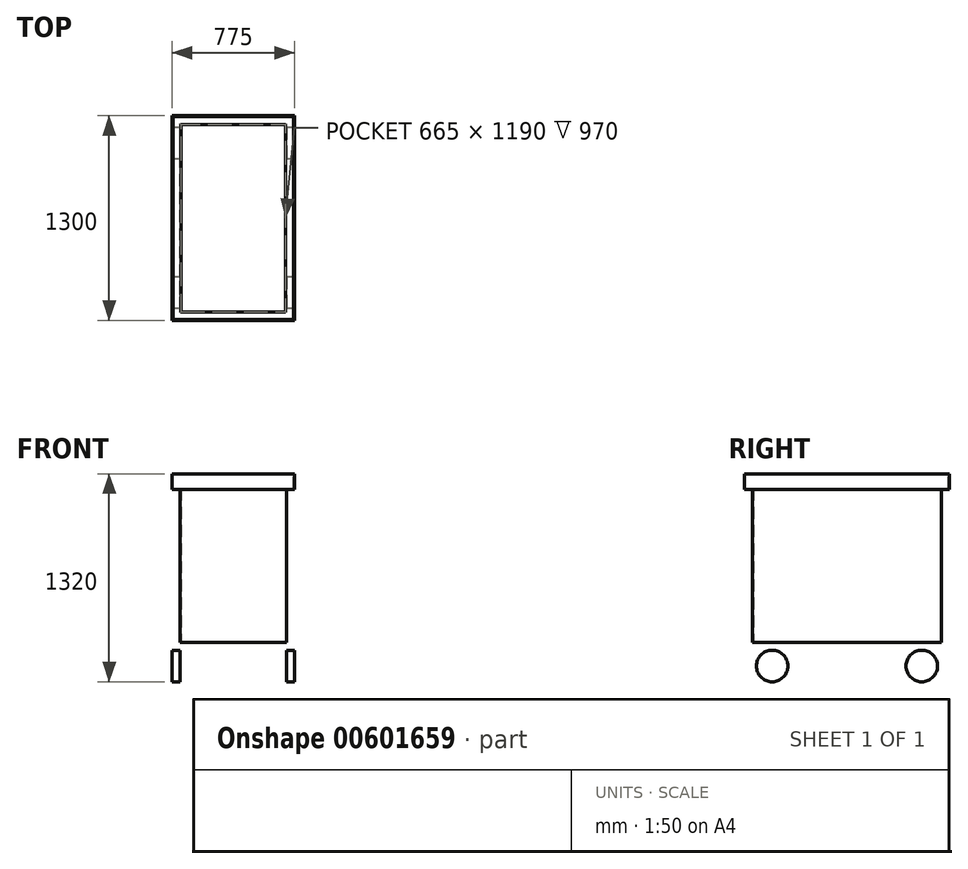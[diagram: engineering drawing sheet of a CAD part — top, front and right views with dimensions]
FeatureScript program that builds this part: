
annotation { "Feature Type Name" : "Feature", "Feature Type Description" : "" }
export const myFeature = defineFeature(function(context is Context, id is Id, definition is map)
    precondition{}
    {
        {
            var Q0;
            Q0=qCreatedBy(makeId("Top.planeOp"),FACE);
            cPlane(context, id + "F0", {"entities" : qUnion([Q0]), "cplaneType" : CPlaneType.OFFSET, "offset" : 250 * mm, "width" : 150 * mm, "height" : 150 * mm});
        }
        {
            var Q0;
            Q0=qCreatedBy(id+"F0.planeOp",FACE);
            var sketch = newSketch(context, id + "F1", { "sketchPlane" : qUnion([Q0])});
            skLineSegment(sketch, "E0.bottom", {"start": v(0, 0) * mm, "end": v(775, 0) * mm});
            skLineSegment(sketch, "E0.top", {"start": v(0, 1300) * mm, "end": v(775, 1300) * mm});
            skLineSegment(sketch, "E0.left", {"start": v(0, 0) * mm, "end": v(0, 1300) * mm});
            skLineSegment(sketch, "E0.right", {"start": v(775, 0) * mm, "end": v(775, 1300) * mm});
            skLineSegment(sketch, "E1.0", {"start": v(50, 50) * mm, "end": v(725, 50) * mm});
            skLineSegment(sketch, "E1.1", {"start": v(50, 50) * mm, "end": v(50, 1250) * mm});
            skLineSegment(sketch, "E1.2", {"start": v(50, 1250) * mm, "end": v(725, 1250) * mm});
            skLineSegment(sketch, "E1.3", {"start": v(725, 50) * mm, "end": v(725, 1250) * mm});
            skSolve(sketch);
        }
        {
            var Q0;
            Q0=makeQuery(id+"F1.imprint","IMPRINT",FACE,{"disambiguationData":[TD([[makeQuery(id+"F1.imprint","IMPRINT",EDGE,{"derivedFrom":sQuery(id+"F1.wireOp",EDGE,"E1.0")}),1.0]])]});
            extrude(context, id + "F2", {"entities" : qUnion([Q0]), "depth" : 1070 * mm, "offsetDistance" : 25 * mm});
        }
        {
            var Q0;
            Q0=makeQuery(id+"F2.opExtrude","CAP_FACE",FACE,{"disambiguationData":[OSD([sQuery(id+"F1.wireOp",EDGE,"E1.0"),sQuery(id+"F1.wireOp",EDGE,"E1.1"),sQuery(id+"F1.wireOp",EDGE,"E1.2"),sQuery(id+"F1.wireOp",EDGE,"E1.3")])],"isStart":false});
            var sketch = newSketch(context, id + "F3", { "sketchPlane" : qUnion([Q0])});
            skLineSegment(sketch, "E2.0", {"start": v(0, 0) * mm, "end": v(775, 0) * mm});
            skLineSegment(sketch, "E3.0", {"start": v(775, 0) * mm, "end": v(775, 1300) * mm});
            skLineSegment(sketch, "E4.0", {"start": v(0, 1300) * mm, "end": v(775, 1300) * mm});
            skLineSegment(sketch, "E5.0", {"start": v(0, 0) * mm, "end": v(0, 1300) * mm});
            skSolve(sketch);
        }
        {
            var Q0;
            Q0=makeQuery(id+"F3.imprint","IMPRINT",FACE,{"disambiguationData":[TD([[makeQuery(id+"F3.imprint","IMPRINT",EDGE,{"derivedFrom":sQuery(id+"F3.wireOp",EDGE,"E2.0")}),1.0]])]});
            extrude(context, id + "F4", {"entities" : qUnion([Q0]), "operationType" : NewBodyOperationType.ADD, "oppositeDirection" : true, "depth" : 100 * mm});
        }
        {
            var Q0;
            {var subQ0=sQuery(id+"F1.wireOp",EDGE,"E1.3");var subQ1=sQuery(id+"F1.wireOp",EDGE,"E1.2");var subQ2=sQuery(id+"F1.wireOp",EDGE,"E1.1");var subQ3=sQuery(id+"F1.wireOp",EDGE,"E1.0");Q0=makeQuery(id+"F4.boolean.opBoolean","MERGE",FACE,{"derivedFrom":[makeQuery(id+"F2.opExtrude","CAP_FACE",FACE,{"disambiguationData":[OSD([subQ3,subQ2,subQ1,subQ0])],"isStart":false}),makeQuery(id+"F4.opExtrude","CAP_FACE",FACE,{"disambiguationData":[OSD([subQ3,subQ2,subQ1,subQ0,sQuery(id+"F3.wireOp",EDGE,"E2.0"),sQuery(id+"F3.wireOp",EDGE,"E3.0"),sQuery(id+"F3.wireOp",EDGE,"E4.0"),sQuery(id+"F3.wireOp",EDGE,"E5.0")])],"isStart":true})]});}
            shell(context, id + "F5", {"entities" : qUnion([Q0]), "thickness" : 5 * mm});
        }
        {
            var Q0;
            Q0=qCreatedBy(makeId("Right.planeOp"),FACE);
            var sketch = newSketch(context, id + "F6", { "sketchPlane" : qUnion([Q0])});
            skCircle(sketch, "E6", {"center": v(1125, 100) * mm, "radius": 100 * mm});
            skCircle(sketch, "E7", {"center": v(175, 100) * mm, "radius": 100 * mm});
            skSolve(sketch);
        }
        {
            var Q0;
            Q0=makeQuery(id+"F6.imprint","IMPRINT",FACE,{"disambiguationData":[TD([[makeQuery(id+"F6.imprint","IMPRINT",EDGE,{"derivedFrom":sQuery(id+"F6.wireOp",EDGE,"E6")}),1.0]])]});
            var Q1;
            Q1=makeQuery(id+"F6.imprint","IMPRINT",FACE,{"disambiguationData":[TD([[makeQuery(id+"F6.imprint","IMPRINT",EDGE,{"derivedFrom":sQuery(id+"F6.wireOp",EDGE,"E7")}),1.0]])]});
            var Q2;
            Q2=makeQuery(id+"F2.opExtrude","SWEPT_FACE",FACE,{"disambiguationData":[OSD([sQuery(id+"F1.wireOp",EDGE,"E1.1")])]});
            extrude(context, id + "F7", {"entities" : qUnion([Q0, Q1]), "operationType" : NewBodyOperationType.ADD, "endBound" : BoundingType.UP_TO_SURFACE, "endBoundEntityFace" : qUnion([Q2]), "depth" : 25 * mm, "offsetDistance" : 25 * mm});
        }
        {
            var Q0;
            Q0=makeQuery(id+"F2.opExtrude","SWEPT_FACE",FACE,{"disambiguationData":[OSD([sQuery(id+"F1.wireOp",EDGE,"E1.3")])]});
            var sketch = newSketch(context, id + "F8", { "sketchPlane" : qUnion([Q0])});
            skCircle(sketch, "E8.0", {"center": v(1125, 100) * mm, "radius": 100 * mm});
            skCircle(sketch, "E9.0", {"center": v(175, 100) * mm, "radius": 100 * mm});
            skSolve(sketch);
        }
        {
            var Q0;
            {var subQ0=sQuery(id+"F8.wireOp",EDGE,"E8.0");var subQ1=sQuery(id+"F1.wireOp",EDGE,"E1.3");var subQ2=makeQuery(id+"F2.opExtrude","CAP_EDGE",EDGE,{"disambiguationData":[OSD([subQ1])],"isStart":true});var subQ3=makeQuery(id+"F8.imprint","INTERSECT",VERTEX,{"derivedFrom":[subQ2,subQ0]});Q0=makeQuery(id+"F8.imprint","IMPRINT",FACE,{"disambiguationData":[TD([[makeQuery(id+"F8.imprint","IMPRINT",EDGE,{"disambiguationData":[TD([[subQ3,-1.0]])],"derivedFrom":subQ0}),1.0]])]});}
            var Q1;
            {var subQ0=sQuery(id+"F8.wireOp",EDGE,"E8.0");var subQ1=sQuery(id+"F1.wireOp",EDGE,"E1.3");var subQ2=makeQuery(id+"F2.opExtrude","CAP_EDGE",EDGE,{"disambiguationData":[OSD([subQ1])],"isStart":true});var subQ3=makeQuery(id+"F8.imprint","INTERSECT",VERTEX,{"derivedFrom":[subQ2,subQ0]});Q1=makeQuery(id+"F8.imprint","IMPRINT",FACE,{"disambiguationData":[TD([[makeQuery(id+"F8.imprint","IMPRINT",EDGE,{"disambiguationData":[TD([[subQ3,1.0]])],"derivedFrom":subQ0}),1.0]])]});}
            var Q2;
            Q2=makeQuery(id+"F8.imprint","IMPRINT",FACE,{"disambiguationData":[TD([[makeQuery(id+"F8.imprint","IMPRINT",EDGE,{"derivedFrom":sQuery(id+"F8.wireOp",EDGE,"E9.0")}),1.0]])]});
            var Q3;
            Q3=makeQuery(id+"F4.opExtrude","SWEPT_FACE",FACE,{"disambiguationData":[OSD([sQuery(id+"F3.wireOp",EDGE,"E3.0")])]});
            extrude(context, id + "F9", {"entities" : qUnion([Q0, Q1, Q2]), "operationType" : NewBodyOperationType.ADD, "endBound" : BoundingType.UP_TO_SURFACE, "endBoundEntityFace" : qUnion([Q3]), "depth" : 25 * mm, "offsetDistance" : 25 * mm});
        }
    });
